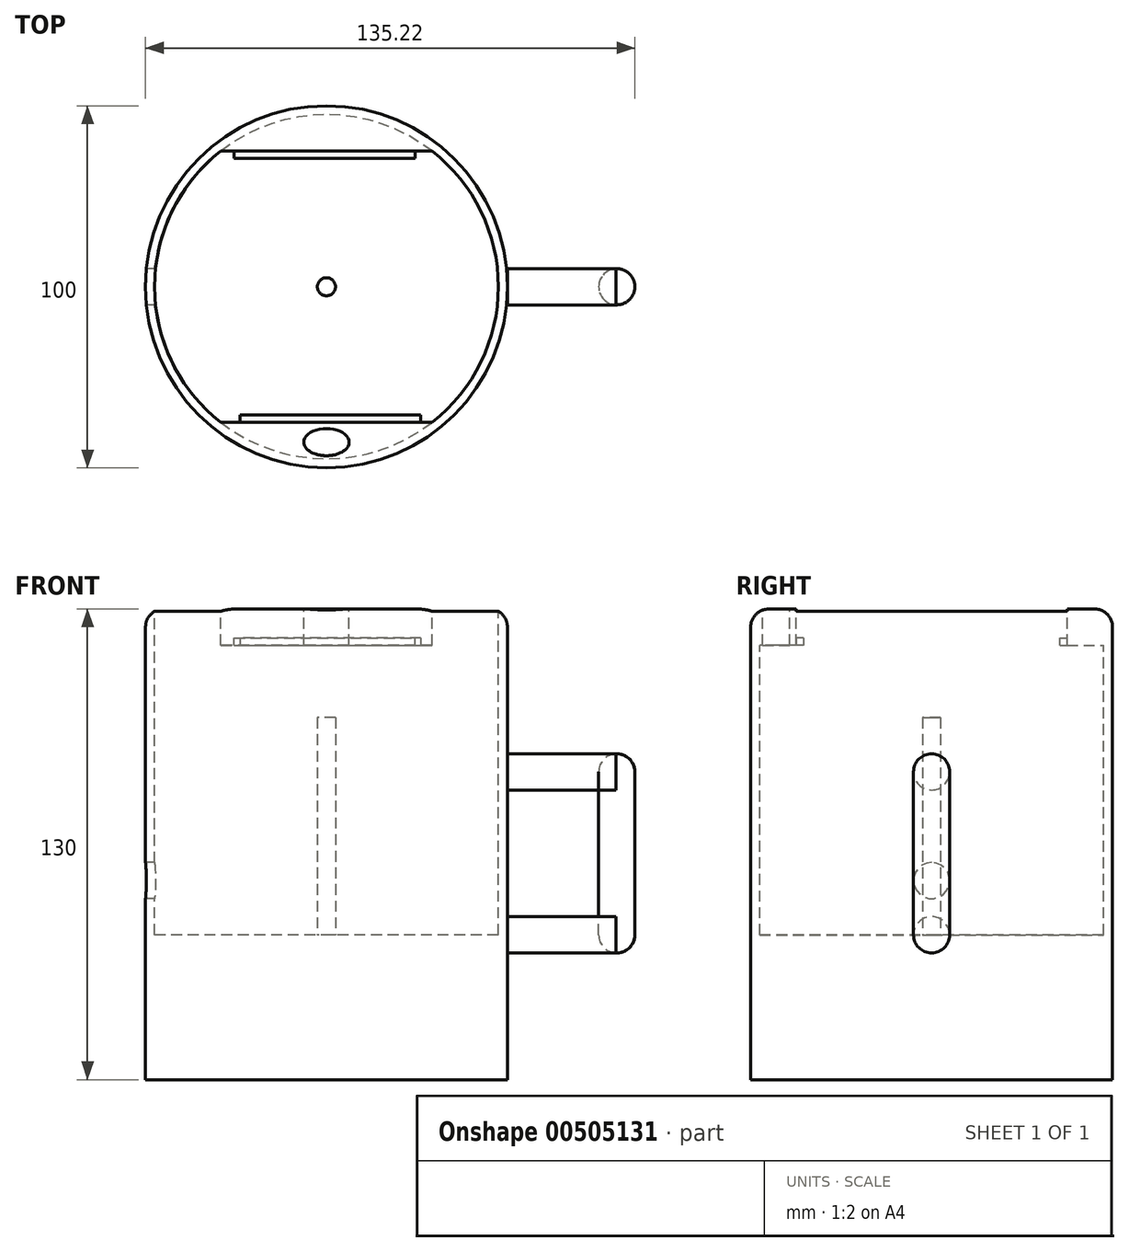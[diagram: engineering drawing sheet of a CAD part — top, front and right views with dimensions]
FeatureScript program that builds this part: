
annotation { "Feature Type Name" : "Feature", "Feature Type Description" : "" }
export const myFeature = defineFeature(function(context is Context, id is Id, definition is map)
    precondition{}
    {
        {
            var Q0;
            Q0=qCreatedBy(makeId("Top.planeOp"),FACE);
            var sketch = newSketch(context, id + "F0", { "sketchPlane" : qUnion([Q0])});
            skCircle(sketch, "E0", {"center": v(0, 0) * mm, "radius": 50 * mm});
            skSolve(sketch);
        }
        {
            var Q0;
            Q0=makeQuery(id+"F0.imprint","IMPRINT",FACE,{"disambiguationData":[TD([[makeQuery(id+"F0.imprint","IMPRINT",EDGE,{"derivedFrom":sQuery(id+"F0.wireOp",EDGE,"E0")}),1.0]])]});
            extrude(context, id + "F1", {"entities" : qUnion([Q0]), "depth" : 130 * mm});
        }
        {
            var Q0;
            Q0=makeQuery(id+"F1.opExtrude","CAP_FACE",FACE,{"disambiguationData":[OSD([sQuery(id+"F0.wireOp",EDGE,"E0")])],"isStart":false});
            var sketch = newSketch(context, id + "F2", { "sketchPlane" : qUnion([Q0])});
            skCircle(sketch, "E1", {"center": v(0, 0) * mm, "radius": 47.5 * mm});
            skSolve(sketch);
        }
        {
            var Q0;
            Q0 = qSketchRegion(id + "F2", true);
            extrude(context, id + "F3", {"entities" : qUnion([Q0]), "operationType" : NewBodyOperationType.REMOVE, "oppositeDirection" : true, "depth" : 90 * mm});
        }
        {
            var Q0;
            Q0=makeQuery(id+"F1.opExtrude","CAP_FACE",FACE,{"disambiguationData":[OSD([sQuery(id+"F0.wireOp",EDGE,"E0")])],"isStart":false});
            var sketch = newSketch(context, id + "F4", { "sketchPlane" : qUnion([Q0])});
            skLineSegment(sketch, "E2", {"start": v(-29.22, -37.45) * mm, "end": v(29.22, -37.45) * mm});
            skSolve(sketch);
        }
        {
            var Q0;
            {var subQ0=sQuery(id+"F4.wireOp",EDGE,"E2");Q0=makeQuery(id+"F4.imprint","IMPRINT",FACE,{"disambiguationData":[TD([[makeQuery(id+"F4.imprint","IMPRINT",EDGE,{"derivedFrom":subQ0}),-1.0]])]});}
            extrude(context, id + "F5", {"entities" : qUnion([Q0]), "operationType" : NewBodyOperationType.ADD, "oppositeDirection" : true, "depth" : 10 * mm});
        }
        {
            var Q0;
            Q0=makeQuery(id+"F5.boolean.opBoolean","MERGE",FACE,{"derivedFrom":[makeQuery(id+"F1.opExtrude","CAP_FACE",FACE,{"disambiguationData":[OSD([sQuery(id+"F0.wireOp",EDGE,"E0")])],"isStart":false}),makeQuery(id+"F5.opExtrude","CAP_FACE",FACE,{"disambiguationData":[OSD([sQuery(id+"F2.wireOp",EDGE,"E1"),sQuery(id+"F4.wireOp",EDGE,"E2")])],"isStart":true})]});
            var sketch = newSketch(context, id + "F6", { "sketchPlane" : qUnion([Q0])});
            skEllipse(sketch, "E3", {"center": v(0, -42.92) * mm, "majorRadius": 6.25 * mm, "minorRadius": 3.75 * mm, "majorAxis": v(-1, 0)});
            skSolve(sketch);
        }
        {
            var Q0;
            Q0 = qSketchRegion(id + "F6", true);
            extrude(context, id + "F7", {"entities" : qUnion([Q0]), "operationType" : NewBodyOperationType.REMOVE, "oppositeDirection" : true, "depth" : 10 * mm});
        }
        {
            var Q0;
            Q0=makeQuery(id+"F5.boolean.opBoolean","MERGE",FACE,{"derivedFrom":[makeQuery(id+"F1.opExtrude","CAP_FACE",FACE,{"disambiguationData":[OSD([sQuery(id+"F0.wireOp",EDGE,"E0")])],"isStart":false}),makeQuery(id+"F5.opExtrude","CAP_FACE",FACE,{"disambiguationData":[OSD([sQuery(id+"F2.wireOp",EDGE,"E1"),sQuery(id+"F4.wireOp",EDGE,"E2")])],"isStart":true})]});
            var sketch = newSketch(context, id + "F8", { "sketchPlane" : qUnion([Q0])});
            skLineSegment(sketch, "E4", {"start": v(-29.22, 37.45) * mm, "end": v(29.22, 37.45) * mm});
            skSolve(sketch);
        }
        {
            var Q0;
            Q0 = qSketchRegion(id + "F8", true);
            var Q1;
            {var subQ0=sQuery(id+"F8.wireOp",EDGE,"E4");Q1=makeQuery(id+"F8.imprint","IMPRINT",FACE,{"disambiguationData":[TD([[makeQuery(id+"F8.imprint","IMPRINT",EDGE,{"derivedFrom":subQ0}),1.0]])]});}
            extrude(context, id + "F9", {"entities" : qUnion([Q0, Q1]), "operationType" : NewBodyOperationType.ADD, "oppositeDirection" : true, "depth" : 10 * mm});
        }
        {
            var Q0;
            Q0=makeQuery(id+"F9.opExtrude","SWEPT_FACE",FACE,{"disambiguationData":[OSD([sQuery(id+"F8.wireOp",EDGE,"E4")])]});
            var sketch = newSketch(context, id + "F10", { "sketchPlane" : qUnion([Q0])});
            skLineSegment(sketch, "E5.bottom", {"start": v(-25.54, 120) * mm, "end": v(24.46, 120) * mm});
            skLineSegment(sketch, "E5.top", {"start": v(-25.54, 122) * mm, "end": v(24.46, 122) * mm});
            skLineSegment(sketch, "E5.left", {"start": v(-25.54, 120) * mm, "end": v(-25.54, 122) * mm});
            skLineSegment(sketch, "E5.right", {"start": v(24.46, 120) * mm, "end": v(24.46, 122) * mm});
            skSolve(sketch);
        }
        {
            var Q0;
            Q0 = qSketchRegion(id + "F10", true);
            extrude(context, id + "F11", {"entities" : qUnion([Q0]), "operationType" : NewBodyOperationType.ADD, "depth" : 2 * mm, "offsetDistance" : 25 * mm});
        }
        {
            var Q0;
            Q0=makeQuery(id+"F1.opExtrude","CAP_EDGE",EDGE,{"disambiguationData":[OSD([sQuery(id+"F0.wireOp",EDGE,"E0")])],"isStart":false});
            fillet(context, id + "F12", {"entities" : qUnion([Q0]), "radius" : 5 * mm, "tangentPropagation" : true, "allowEdgeOverflow" : false});
        }
        {
            var Q0;
            Q0=qCreatedBy(makeId("Right.planeOp"),FACE);
            cPlane(context, id + "F13", {"entities" : qUnion([Q0]), "cplaneType" : CPlaneType.OFFSET, "offset" : 50 * mm, "width" : 150 * mm, "height" : 150 * mm});
        }
        {
            var Q0;
            Q0=qCreatedBy(id+"F13.planeOp",FACE);
            var sketch = newSketch(context, id + "F14", { "sketchPlane" : qUnion([Q0])});
            skCircle(sketch, "E6", {"center": v(0, 85) * mm, "radius": 5 * mm});
            skCircle(sketch, "E7", {"center": v(0, 40) * mm, "radius": 5 * mm});
            skSolve(sketch);
        }
        {
            var Q0;
            Q0=makeQuery(id+"F14.imprint","IMPRINT",FACE,{"disambiguationData":[TD([[makeQuery(id+"F14.imprint","IMPRINT",EDGE,{"derivedFrom":sQuery(id+"F14.wireOp",EDGE,"E6")}),1.0]])]});
            var Q1;
            Q1=makeQuery(id+"F14.imprint","IMPRINT",FACE,{"disambiguationData":[TD([[makeQuery(id+"F14.imprint","IMPRINT",EDGE,{"derivedFrom":sQuery(id+"F14.wireOp",EDGE,"E7")}),1.0]])]});
            extrude(context, id + "F15", {"entities" : qUnion([Q0, Q1]), "operationType" : NewBodyOperationType.ADD, "depth" : 30 * mm});
        }
        {
            var Q0;
            Q0=qCreatedBy(makeId("Top.planeOp"),FACE);
            cPlane(context, id + "F16", {"entities" : qUnion([Q0]), "cplaneType" : CPlaneType.OFFSET, "offset" : 50 * mm, "width" : 150 * mm, "height" : 150 * mm});
        }
        {
            var Q0;
            Q0=qCreatedBy(makeId("Right.planeOp"),FACE);
            cPlane(context, id + "F17", {"entities" : qUnion([Q0]), "cplaneType" : CPlaneType.OFFSET, "offset" : 50 * mm, "oppositeDirection" : true, "width" : 150 * mm, "height" : 150 * mm});
        }
        {
            var Q0;
            Q0=qCreatedBy(id+"F17.planeOp",FACE);
            var sketch = newSketch(context, id + "F18", { "sketchPlane" : qUnion([Q0])});
            skCircle(sketch, "E8", {"center": v(0, 55) * mm, "radius": 5 * mm});
            skSolve(sketch);
        }
        {
            var Q0;
            Q0=qCreatedBy(makeId("Top.planeOp"),FACE);
            cPlane(context, id + "F19", {"entities" : qUnion([Q0]), "cplaneType" : CPlaneType.OFFSET, "offset" : 90 * mm, "width" : 150 * mm, "height" : 150 * mm});
        }
        {
            var Q0;
            Q0=qCreatedBy(id+"F19.planeOp",FACE);
            var sketch = newSketch(context, id + "F20", { "sketchPlane" : qUnion([Q0])});
            skCircle(sketch, "E9", {"center": v(80.22, 0) * mm, "radius": 5 * mm});
            skSolve(sketch);
        }
        {
            var Q0;
            Q0=makeQuery(id+"F20.imprint","IMPRINT",FACE,{"disambiguationData":[TD([[makeQuery(id+"F20.imprint","IMPRINT",EDGE,{"derivedFrom":sQuery(id+"F20.wireOp",EDGE,"E9")}),1.0]])]});
            extrude(context, id + "F21", {"entities" : qUnion([Q0]), "oppositeDirection" : true, "depth" : 55 * mm});
        }
        {
            var Q0;
            Q0=makeQuery(id+"F21.opExtrude","CAP_EDGE",EDGE,{"disambiguationData":[OSD([sQuery(id+"F20.wireOp",EDGE,"E9")])],"isStart":false});
            var Q1;
            Q1=makeQuery(id+"F21.opExtrude","CAP_EDGE",EDGE,{"disambiguationData":[OSD([sQuery(id+"F20.wireOp",EDGE,"E9")])],"isStart":true});
            var Q2;
            Q2=makeQuery(id+"F21.opExtrude","SWEPT_FACE",FACE,{"disambiguationData":[OSD([sQuery(id+"F20.wireOp",EDGE,"E9")])]});
            fillet(context, id + "F22", {"entities" : qUnion([Q0, Q1, Q2]), "radius" : 5 * mm, "tangentPropagation" : true, "allowEdgeOverflow" : false});
        }
        {
            var Q0;
            Q0 = qSketchRegion(id + "F18", true);
            extrude(context, id + "F23", {"entities" : qUnion([Q0]), "operationType" : NewBodyOperationType.REMOVE, "depth" : 25 * mm, "offsetDistance" : 25 * mm});
        }
        {
            var Q0;
            Q0=makeQuery(id+"F5.opExtrude","SWEPT_FACE",FACE,{"disambiguationData":[OSD([sQuery(id+"F4.wireOp",EDGE,"E2")])]});
            var sketch = newSketch(context, id + "F24", { "sketchPlane" : qUnion([Q0])});
            skPoint(sketch, "E10.endSnap0", {"position": v(29.22, 124.67) * mm});
            skLineSegment(sketch, "E11", {"start": v(-26.07, 122) * mm, "end": v(-26.07, 120) * mm});
            skLineSegment(sketch, "E12", {"start": v(-26.07, 122) * mm, "end": v(23.93, 122) * mm});
            skLineSegment(sketch, "E13", {"start": v(23.93, 122) * mm, "end": v(23.93, 120) * mm});
            skLineSegment(sketch, "E14", {"start": v(23.93, 120) * mm, "end": v(-26.07, 120) * mm});
            skSolve(sketch);
        }
        {
            var Q0;
            Q0 = qSketchRegion(id + "F24", true);
            extrude(context, id + "F25", {"entities" : qUnion([Q0]), "operationType" : NewBodyOperationType.ADD, "depth" : 2 * mm, "offsetDistance" : 25 * mm});
        }
        {
            var Q0;
            Q0=makeQuery(id+"F3.boolean.opBoolean","COPY",FACE,{"derivedFrom":makeQuery(id+"F3.opExtrude","CAP_FACE",FACE,{"disambiguationData":[OSD([sQuery(id+"F2.wireOp",EDGE,"E1")])],"isStart":false})});
            var sketch = newSketch(context, id + "F26", { "sketchPlane" : qUnion([Q0])});
            skCircle(sketch, "E15", {"center": v(0, 0) * mm, "radius": 2.5 * mm});
            skSolve(sketch);
        }
        {
            var Q0;
            Q0 = qSketchRegion(id + "F26", true);
            extrude(context, id + "F27", {"entities" : qUnion([Q0]), "operationType" : NewBodyOperationType.ADD, "depth" : 60 * mm, "offsetDistance" : 25 * mm});
        }
    });
